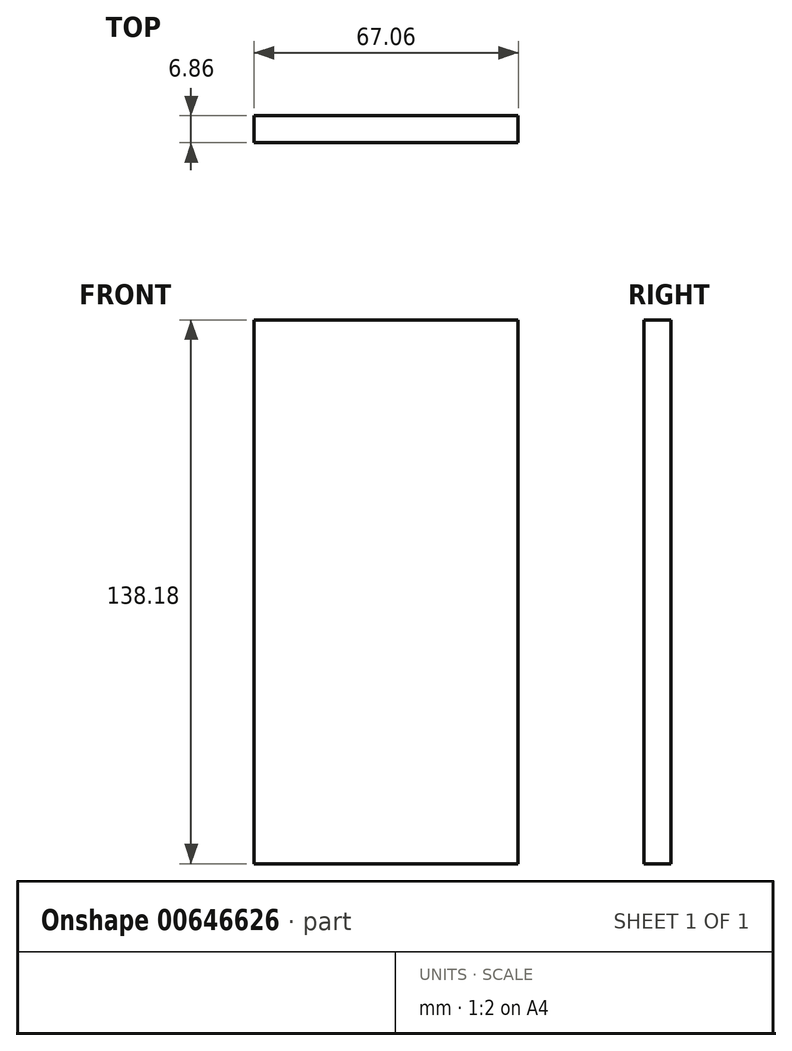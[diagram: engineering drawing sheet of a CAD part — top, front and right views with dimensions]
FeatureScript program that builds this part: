
annotation { "Feature Type Name" : "Feature", "Feature Type Description" : "" }
export const myFeature = defineFeature(function(context is Context, id is Id, definition is map)
    precondition{}
    {
        {
            var Q0;
            Q0=qCreatedBy(makeId("Front.planeOp"),FACE);
            var sketch = newSketch(context, id + "F0", { "sketchPlane" : qUnion([Q0])});
            skLineSegment(sketch, "E0.bottom", {"start": v(0, 0) * mm, "end": v(67.06, 0) * mm});
            skLineSegment(sketch, "E0.top", {"start": v(0, 138.18) * mm, "end": v(67.06, 138.18) * mm});
            skLineSegment(sketch, "E0.left", {"start": v(0, 0) * mm, "end": v(0, 138.18) * mm});
            skLineSegment(sketch, "E0.right", {"start": v(67.06, 0) * mm, "end": v(67.06, 138.18) * mm});
            skSolve(sketch);
        }
        {
            var Q0;
            Q0=makeQuery(id+"F0.imprint","IMPRINT",FACE,{"disambiguationData":[TD([[makeQuery(id+"F0.imprint","IMPRINT",EDGE,{"derivedFrom":sQuery(id+"F0.wireOp",EDGE,"E0.bottom")}),1.0]])]});
            extrude(context, id + "F1", {"entities" : qUnion([Q0]), "depth" : 6.86 * mm, "offsetDistance" : 25.4 * mm});
        }
    });
